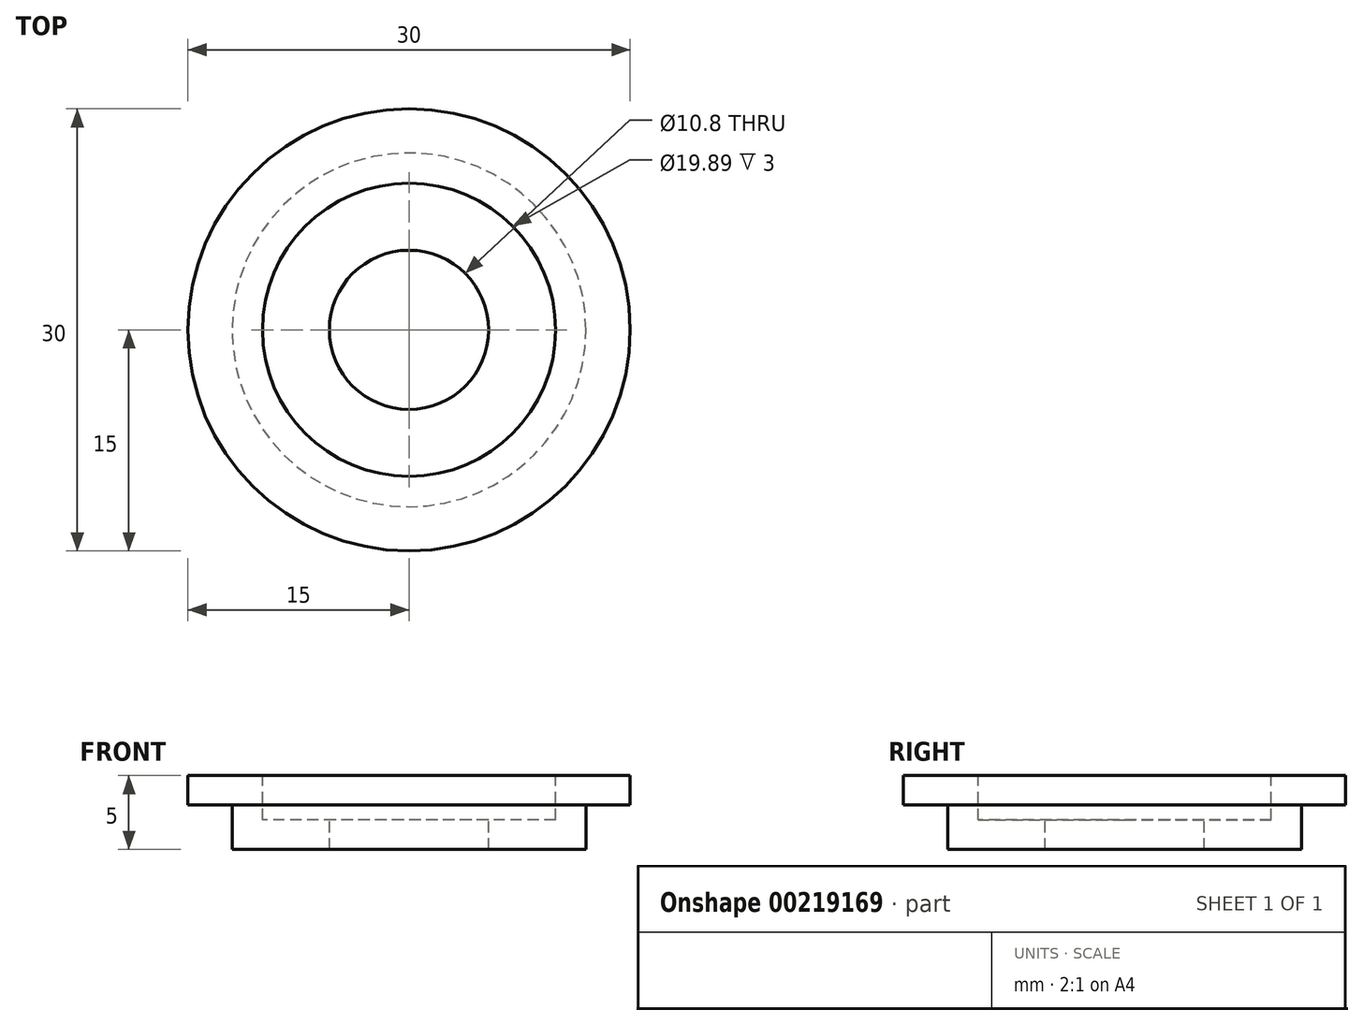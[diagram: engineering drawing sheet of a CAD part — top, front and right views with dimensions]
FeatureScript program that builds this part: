
annotation { "Feature Type Name" : "Feature", "Feature Type Description" : "" }
export const myFeature = defineFeature(function(context is Context, id is Id, definition is map)
    precondition{}
    {
        {
            var Q0;
            Q0=qCreatedBy(makeId("Front.planeOp"),FACE);
            var sketch = newSketch(context, id + "F0", { "sketchPlane" : qUnion([Q0])});
            skLineSegment(sketch, "E0", {"start": v(0, 19.7) * mm, "end": v(0, -25.3) * mm, "construction": true});
            skLineSegment(sketch, "E1", {"start": v(5.4, 0) * mm, "end": v(12, 0) * mm});
            skLineSegment(sketch, "E2", {"start": v(12, 0) * mm, "end": v(12, 3) * mm});
            skLineSegment(sketch, "E3", {"start": v(12, 3) * mm, "end": v(15, 3) * mm});
            skLineSegment(sketch, "E4", {"start": v(15, 3) * mm, "end": v(15, 5) * mm});
            skLineSegment(sketch, "E5", {"start": v(15, 5) * mm, "end": v(9.94, 5) * mm});
            skLineSegment(sketch, "E6", {"start": v(9.94, 5) * mm, "end": v(9.94, 2) * mm});
            skLineSegment(sketch, "E7", {"start": v(9.94, 2) * mm, "end": v(5.4, 2) * mm});
            skLineSegment(sketch, "E8", {"start": v(5.4, 2) * mm, "end": v(5.4, 0) * mm});
            skSolve(sketch);
        }
        {
            var Q0;
            Q0=makeQuery(id+"F0.imprint","IMPRINT",FACE,{"disambiguationData":[TD([[makeQuery(id+"F0.imprint","IMPRINT",EDGE,{"derivedFrom":sQuery(id+"F0.wireOp",EDGE,"E1")}),1.0]])]});
            var Q1;
            Q1=sQuery(id+"F0.wireOp",EDGE,"E0");
            revolve(context, id + "F1", {"entities" : qUnion([Q0]), "axis" : qUnion([Q1]), "revolveType" : RevolveType.FULL});
        }
    });
